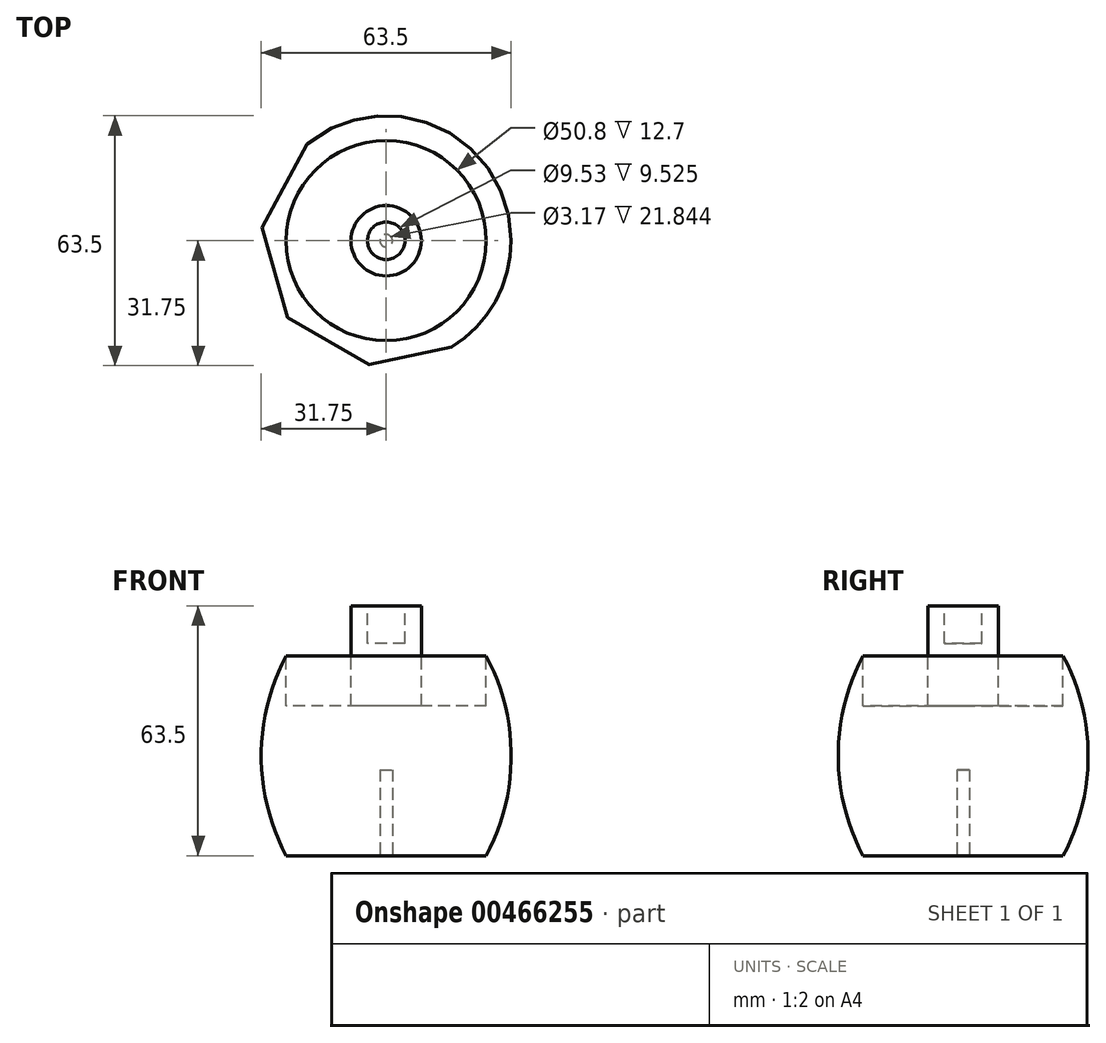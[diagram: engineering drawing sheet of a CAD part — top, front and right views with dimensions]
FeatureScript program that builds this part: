
annotation { "Feature Type Name" : "Feature", "Feature Type Description" : "" }
export const myFeature = defineFeature(function(context is Context, id is Id, definition is map)
    precondition{}
    {
        {
            var Q0;
            Q0=qCreatedBy(makeId("Front.planeOp"),FACE);
            var sketch = newSketch(context, id + "F0", { "sketchPlane" : qUnion([Q0])});
            skLineSegment(sketch, "E0", {"start": v(0, 0) * mm, "end": v(25.4, 0) * mm});
            skLineSegment(sketch, "E1", {"start": v(8.93, 50.8) * mm, "end": v(8.93, 63.5) * mm});
            skLineSegment(sketch, "E2", {"start": v(8.93, 63.5) * mm, "end": v(0, 63.5) * mm});
            skLineSegment(sketch, "E3", {"start": v(0, 63.5) * mm, "end": v(0, 0) * mm});
            skLineSegment(sketch, "E4", {"start": v(25.4, 50.8) * mm, "end": v(8.93, 50.8) * mm});
            skArc(sketch, "E5", {"start": v(25.4, 0) * mm, "mid": v(31.75, 25.4) * mm, "end": v(25.4, 50.8) * mm});
            skPoint(sketch, "E6", {"position": v(31.75, 25.4) * mm});
            skPoint(sketch, "E7", {"position": v(25.4, 25.4) * mm});
            skPoint(sketch, "E8", {"position": v(8.93, 0) * mm});
            skSolve(sketch);
        }
        {
            var Q0;
            Q0 = qSketchRegion(id + "F0", true);
            var Q1;
            Q1=sQuery(id+"F0.wireOp",EDGE,"E3");
            revolve(context, id + "F1", {"entities" : qUnion([Q0]), "axis" : qUnion([Q1]), "revolveType" : RevolveType.FULL});
        }
        {
            var Q0;
            Q0=makeQuery(id+"F1.opRevolve","SWEPT_FACE",FACE,{"disambiguationData":[OSD([sQuery(id+"F0.wireOp",EDGE,"E2")])]});
            var sketch = newSketch(context, id + "F2", { "sketchPlane" : qUnion([Q0])});
            skCircle(sketch, "E9", {"center": v(0, 0) * mm, "radius": 4.76 * mm});
            skSolve(sketch);
        }
        {
            var Q0;
            Q0=makeQuery(id+"F1.opRevolve","SWEPT_FACE",FACE,{"disambiguationData":[OSD([sQuery(id+"F0.wireOp",EDGE,"E4")])]});
            extrude(context, id + "F3", {"entities" : qUnion([Q0]), "operationType" : NewBodyOperationType.REMOVE, "oppositeDirection" : true, "depth" : 12.7 * mm});
        }
        {
            var Q0;
            Q0=makeQuery(id+"F2.imprint","IMPRINT",FACE,{"disambiguationData":[TD([[makeQuery(id+"F2.imprint","IMPRINT",EDGE,{"derivedFrom":sQuery(id+"F2.wireOp",EDGE,"E9")}),1.0]])]});
            var Q1;
            Q1=sQuery(id+"F2.wireOp",EDGE,"E9");
            extrude(context, id + "F4", {"entities" : qUnion([Q0]), "operationType" : NewBodyOperationType.REMOVE, "surfaceEntities" : qUnion([Q1]), "oppositeDirection" : true, "depth" : 9.52 * mm});
        }
        {
            var Q0;
            Q0=makeQuery(id+"F1.opRevolve","SWEPT_FACE",FACE,{"disambiguationData":[OSD([sQuery(id+"F0.wireOp",EDGE,"E0")])]});
            var sketch = newSketch(context, id + "F5", { "sketchPlane" : qUnion([Q0])});
            skCircle(sketch, "E10", {"center": v(0, 0) * mm, "radius": 1.59 * mm});
            skSolve(sketch);
        }
        {
            var Q0;
            Q0=makeQuery(id+"F5.imprint","IMPRINT",FACE,{"disambiguationData":[TD([[makeQuery(id+"F5.imprint","IMPRINT",EDGE,{"derivedFrom":sQuery(id+"F5.wireOp",EDGE,"E10")}),1.0]])]});
            var Q1;
            Q1=sQuery(id+"F5.wireOp",EDGE,"E10");
            extrude(context, id + "F6", {"entities" : qUnion([Q0]), "operationType" : NewBodyOperationType.REMOVE, "surfaceEntities" : qUnion([Q1]), "oppositeDirection" : true, "depth" : 21.84 * mm});
        }
    });
